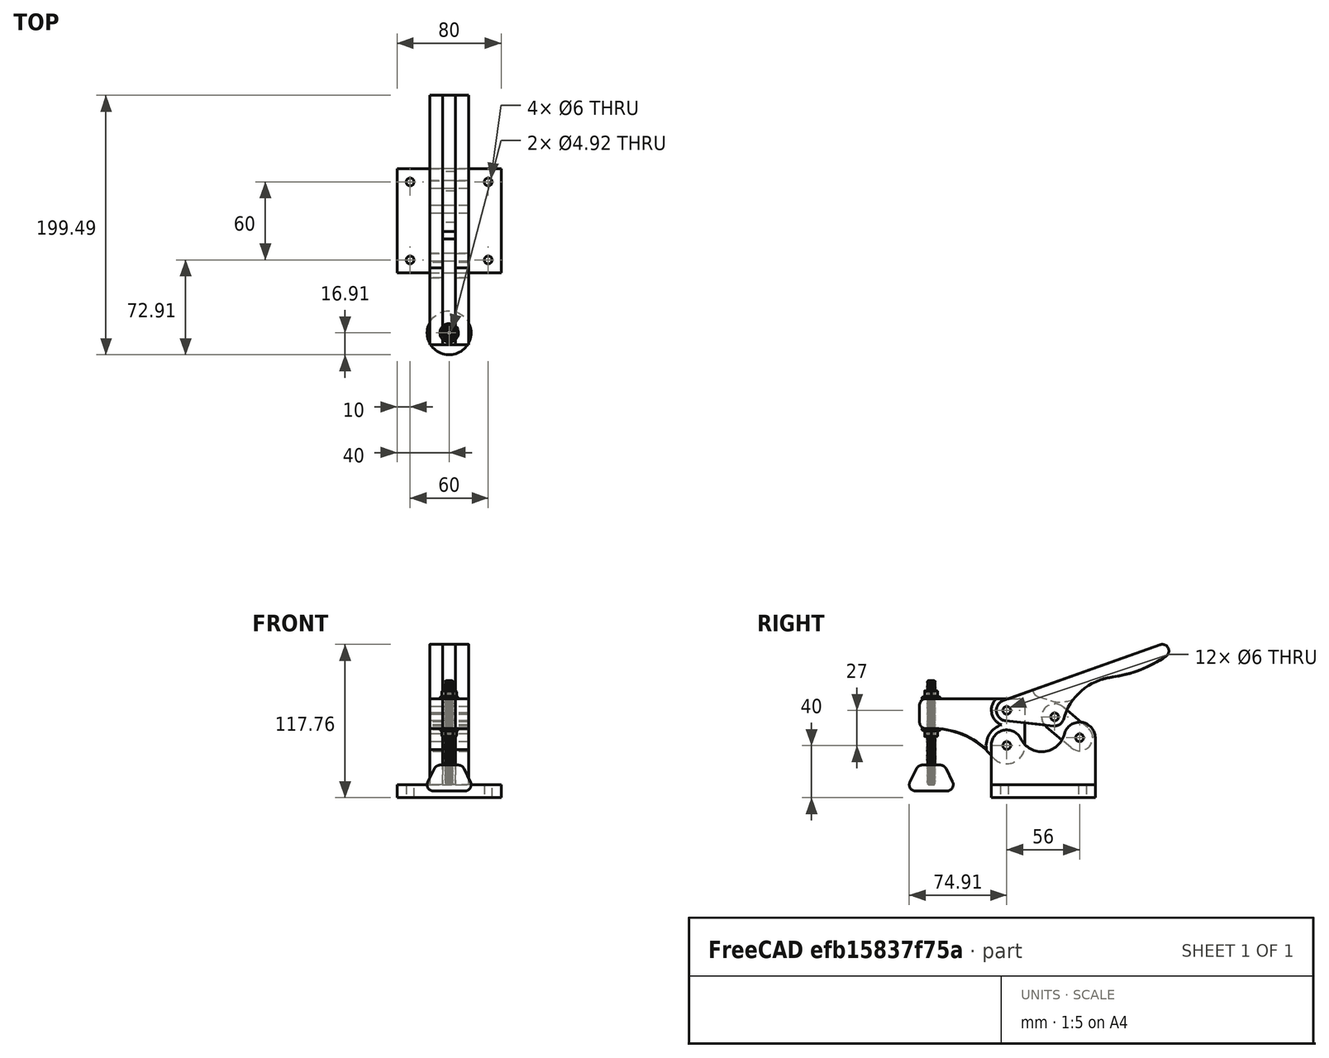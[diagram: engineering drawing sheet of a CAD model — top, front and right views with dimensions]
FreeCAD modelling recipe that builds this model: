
FCSTD DOCUMENT  (FreeCAD 0.19R23756 (Git))
Label: CLAMP CJ
License: Creative Commons Attribution-NonCommercial
LicenseURL: http://creativecommons.org/licenses/by-nc/4.0/
objects: Part::FeaturePython×13, Part::Cylinder×4, Part::Compound×3, Part::Cone×1, Part::Fillet×1
note: 22 computed .brp shape members not serialized (recipe doc carries the construction recipe); baked Part::Feature solids carry a one-line shape summary decoded from their .brp

FEATURE [Part::FeaturePython] b_CLAMP_1_001_  label="CLAMP_1_001"  # a2plus imported part (geometry in sourceFile) (typed FeaturePython)
  a2p_Version = V0.1
  fixedPosition = true
  objectType = a2pPart
  sourceFile = ./CLAMP_1.FCStd
  subassemblyImport = false
  timeLastImport = 1.61442e+09
  updateColors = true
FEATURE [Part::FeaturePython] b_CLAMP_2_001_  label="CLAMP_2_001"  # a2plus imported part (geometry in sourceFile) (typed FeaturePython)
  Placement = pos=(5,-40,10) rot=(-0.57735,-0.57735,-0.57735;4.18879rad)
  a2p_Version = V0.1
  fixedPosition = false
  objectType = a2pPart
  sourceFile = ./CLAMP_2.FCStd
  subassemblyImport = false
  timeLastImport = 1.61442e+09
  updateColors = true
FEATURE [Part::FeaturePython] b_CLAMP_2_001_001  label="CLAMP_2_002"  # a2plus imported part (geometry in sourceFile) (typed FeaturePython)
  Placement = pos=(-15,-40,10) rot=(0.57735,0.57735,0.57735;2.0944rad)
  a2p_Version = V0.1
  fixedPosition = false
  objectType = a2pPart
  sourceFile = ./CLAMP_2.FCStd
  subassemblyImport = false
  timeLastImport = 1.61442e+09
  updateColors = true
FEATURE [Part::Cylinder] Cylinder
  Angle = 360
  AttacherType = Attacher::AttachEngine3D
  Height = 30
  Placement = pos=(15,-28,40) rot=(0,1,0;4.71239rad)
  Radius = 3
FEATURE [Part::Cylinder] Cylinder001
  Angle = 360
  AttacherType = Attacher::AttachEngine3D
  Height = 30
  Placement = pos=(15,28,46) rot=(0,-1,0;1.5708rad)
  Radius = 3
FEATURE [Part::Compound] Compound
  Links = -> [Cylinder001,Cylinder,b_CLAMP_2_001_001,b_CLAMP_2_001_,b_CLAMP_1_001_]
FEATURE [Part::FeaturePython] b_CLAMP_3_001_  label="CLAMP_3_001"  # a2plus imported part (geometry in sourceFile) (typed FeaturePython)
  Placement = pos=(5,128,8) rot=(0,1,0;4.71239rad)
  a2p_Version = V0.1
  fixedPosition = false
  objectType = a2pPart
  sourceFile = ./CLAMP_3.FCStd
  subassemblyImport = false
  timeLastImport = 1.61442e+09
  updateColors = true
FEATURE [Part::FeaturePython] b_CLAMP_4_001_  label="CLAMP_4_001"  # a2plus imported part (geometry in sourceFile) (typed FeaturePython)
  Placement = pos=(5,-1.1e-15,1.1e-15) rot=(0.57735,0.57735,0.57735;2.0944rad)
  a2p_Version = V0.1
  fixedPosition = false
  objectType = a2pPart
  sourceFile = ./CLAMP_4.FCStd
  subassemblyImport = false
  timeLastImport = 1.61442e+09
  updateColors = true
FEATURE [Part::FeaturePython] b_CLAMP_4_001_001  label="CLAMP_4_002"  # a2plus imported part (geometry in sourceFile) (typed FeaturePython)
  Placement = pos=(-15,-1e-15,1e-15) rot=(0.57735,0.57735,0.57735;2.0944rad)
  a2p_Version = V0.1
  fixedPosition = false
  objectType = a2pPart
  sourceFile = ./CLAMP_4.FCStd
  subassemblyImport = false
  timeLastImport = 1.61442e+09
  updateColors = true
FEATURE [Part::Cylinder] Cylinder002
  Angle = 360
  AttacherType = Attacher::AttachEngine3D
  Height = 30
  Placement = pos=(15,0,3.3e-15) rot=(0,1,0;4.71239rad)
  Radius = 3
FEATURE [Part::Cylinder] Cylinder003
  Angle = 360
  AttacherType = Attacher::AttachEngine3D
  Height = 30
  Placement = pos=(15,33,-17) rot=(0,-1,0;1.5708rad)
  Radius = 3
FEATURE [Part::Compound] Compound001
  Links = -> [Cylinder003,Cylinder002,b_CLAMP_4_001_001,b_CLAMP_4_001_,b_CLAMP_3_001_]
  Placement = pos=(0,-28,67) rot=(1,0,0;0.342085rad)
FEATURE [Part::FeaturePython] b_CLAMP_5_001_  label="CLAMP_5_001"  # a2plus imported part (geometry in sourceFile) (typed FeaturePython)
  Placement = pos=(-5,28,46) rot=(0.684791,0.249244,0.684791;2.65306rad)
  a2p_Version = V0.1
  fixedPosition = false
  objectType = a2pPart
  sourceFile = ./CLAMP_5.FCStd
  subassemblyImport = false
  timeLastImport = 1.61442e+09
  updateColors = true
FEATURE [Part::FeaturePython] b_CLAMP_6_001_  label="CLAMP_6_001"  # a2plus imported part (geometry in sourceFile) (typed FeaturePython)
  Placement = pos=(-5,0,-1.1e-15) rot=(0,1,0;1.5708rad)
  a2p_Version = V0.1
  fixedPosition = false
  objectType = a2pPart
  sourceFile = ./CLAMP_6.FCStd
  subassemblyImport = false
  timeLastImport = 1.61442e+09
  updateColors = true
FEATURE [Part::FeaturePython] b_CLAMP_7_001_  label="CLAMP_7_001"  # a2plus imported part (geometry in sourceFile) (typed FeaturePython)
  Placement = pos=(-5,-8,36) rot=(-0.57735,0.57735,0.57735;4.18879rad)
  a2p_Version = V0.1
  fixedPosition = false
  objectType = a2pPart
  sourceFile = ./CLAMP_7.FCStd
  subassemblyImport = false
  timeLastImport = 1.61442e+09
  updateColors = true
FEATURE [Part::FeaturePython] b_CLAMP_7_001_001  label="CLAMP_7_002"  # a2plus imported part (geometry in sourceFile) (typed FeaturePython)
  Placement = pos=(15,-8,36) rot=(0.57735,-0.57735,-0.57735;2.0944rad)
  a2p_Version = V0.1
  fixedPosition = false
  objectType = a2pPart
  sourceFile = ./CLAMP_7.FCStd
  subassemblyImport = false
  timeLastImport = 1.61442e+09
  updateColors = true
FEATURE [Part::Cone] Cone
  Angle = 360
  AttacherType = Attacher::AttachEngine3D
  Height = 20
  Placement = pos=(0,-58,-35) rot=(0,0,1;0rad)
  Radius1 = 20
  Radius2 = 10
FEATURE [Part::Fillet] Fillet
  Base = -> Cone
  Edges = 2 edges r=5: [Edge1,Edge3]
FEATURE [Part::FeaturePython] ThreadedRod  label="M6x80.0-ThreadedRod"  # Fasteners workbench fastener (typed FeaturePython)
  Placement = pos=(0,-58,-30) rot=(1,0,0;3.14159rad)
  diameter = 8
  invert = false
  length = 80
  matchOuter = false
  offset = 32
  thread = true
FEATURE [Part::FeaturePython] Nut  label="M6-Nut"  # Fasteners workbench fastener (typed FeaturePython)
  Placement = pos=(0,-58,13) rot=(-1,0,0;3.14159rad)
  baseObject = -> ThreadedRod [Edge655]
  diameter = 2
  invert = false
  matchOuter = false
  offset = 37
  thread = false
  type = 6
FEATURE [Part::FeaturePython] Clone  label="M6-Nut001"  # Draft clone (typed FeaturePython)
  AttacherType = Attacher::AttachEngine3D
  Fuse = false
  Objects = -> [Nut]
  Placement = pos=(4e-15,-58,36) rot=(0,0,-1;3.14159rad)
  Scale = (1,1,1)
FEATURE [Part::Compound] Compound002
  Links = -> [Clone,Nut,ThreadedRod,Fillet,b_CLAMP_7_001_001,b_CLAMP_7_001_,b_CLAMP_6_001_]
  Placement = pos=(0,-28,40) rot=(0,0,1;0rad)
